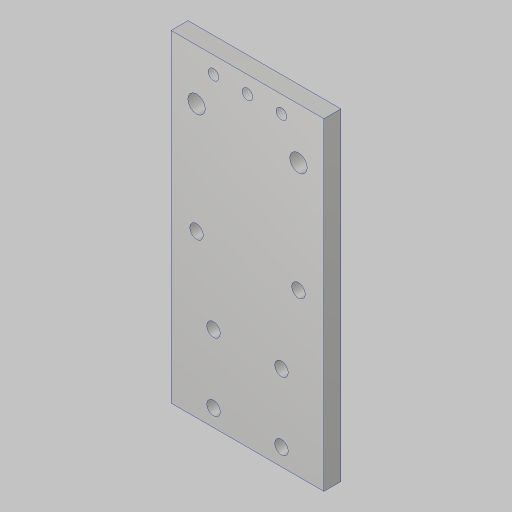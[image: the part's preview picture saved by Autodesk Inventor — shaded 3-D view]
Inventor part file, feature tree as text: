
AUTODESK INVENTOR PART (.ipt)
format: ipt  version: 2023.5 (Build 275446000, 446)  size: 142,336 bytes
history: native  units: in
note: dims shown in document units (in); Inventor stores cm internally (conversion verified against a paired STEP export)
features: hole x3, sketch x2, extrude x1
ambient origin geometry x8: Origin, YZ Plane, XZ Plane, XY Plane, X Axis, Y Axis, Z Axis, Center Point
bodies: Solid1 (feature_tree)
feature tree (6):
  sketch  "Sketch1"  dims[d0=0.257in d1=1.5in]
  extrude  "Extrusion1"  Depth=1.5in
  hole  "Hole1"  [1 undecoded]
  hole  "Hole2"  [1 undecoded]
  hole  "Hole3"  [1 undecoded]
  sketch  "Sketch2"  dims[d4=4.0in d6=0.25in d7=0.0in d8=1.5in d9=2.375in d10=0.201in d11=0.75in d12=0.385in d13=0.25in d14=0.5635in d15=1.0in d16=0.8108in d17=6.0in d18=2.25in d19=0.25in d20=4.75in d21=1.0in d22=0.156in d23=0.38in d24=0.385in d25=0.25in d26=0.5635in d27=1.0in d28=0.8108in d29=0.25in d32=1.0in d33=1.0in d34=0.25in d35=0.201in d36=0.38in d37=0.385in d38=0.25in d39=0.5635in d40=1.0in d41=0.8108in d42=0.5in d43=0.75in]
note: 3 required parameter values undecoded (feature->parameter linkage not recoverable at this tier; creation-order binding heuristic only, values carry confidence <= 0.55)
